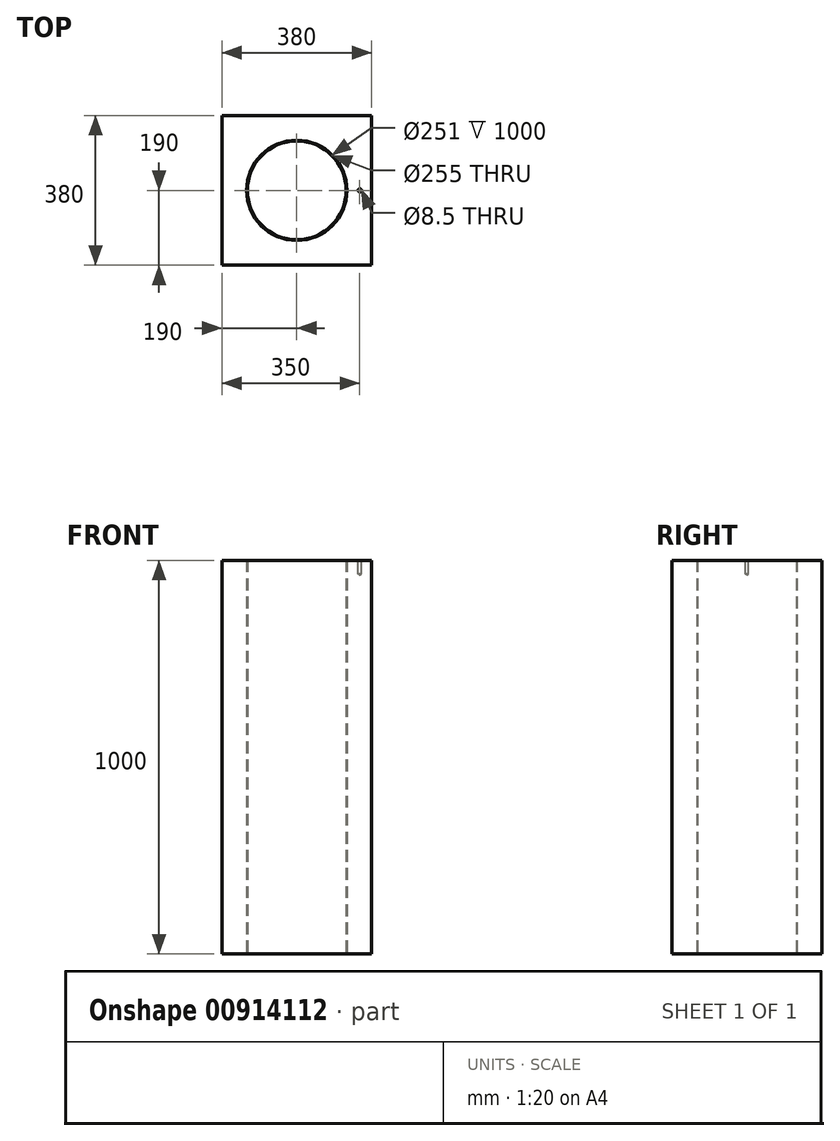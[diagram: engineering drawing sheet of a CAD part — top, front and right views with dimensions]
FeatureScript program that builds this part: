
annotation { "Feature Type Name" : "Feature", "Feature Type Description" : "" }
export const myFeature = defineFeature(function(context is Context, id is Id, definition is map)
    precondition{}
    {
        {
            var Q0;
            Q0=qCreatedBy(makeId("Top.planeOp"),FACE);
            var sketch = newSketch(context, id + "F0", { "sketchPlane" : qUnion([Q0])});
            skCircle(sketch, "E0", {"center": v(0, 0) * mm, "radius": 127.5 * mm});
            skLineSegment(sketch, "E1.bottom", {"start": v(190, -190) * mm, "end": v(-190, -190) * mm});
            skLineSegment(sketch, "E1.top", {"start": v(190, 190) * mm, "end": v(-190, 190) * mm});
            skLineSegment(sketch, "E1.left", {"start": v(190, -190) * mm, "end": v(190, 190) * mm});
            skLineSegment(sketch, "E1.right", {"start": v(-190, -190) * mm, "end": v(-190, 190) * mm});
            skSolve(sketch);
        }
        {
            var Q0;
            Q0=makeQuery(id+"F0.imprint","IMPRINT",FACE,{"disambiguationData":[TD([[makeQuery(id+"F0.imprint","IMPRINT",EDGE,{"derivedFrom":sQuery(id+"F0.wireOp",EDGE,"E0")}),-1.0]])]});
            extrude(context, id + "F1", {"entities" : qUnion([Q0]), "depth" : 1000 * mm, "offsetDistance" : 25 * mm});
        }
        {
            var Q0;
            Q0=makeQuery(id+"F1.opExtrude","CAP_FACE",FACE,{"disambiguationData":[OSD([sQuery(id+"F0.wireOp",EDGE,"E0"),sQuery(id+"F0.wireOp",EDGE,"11AzcM2P-MoAo-TPdU-SA0A-KGDendb4HZRf")])],"isStart":false});
            var sketch = newSketch(context, id + "F2", { "sketchPlane" : qUnion([Q0])});
            skPoint(sketch, "E2", {"position": v(160, 0) * mm});
            skLineSegment(sketch, "E3", {"start": v(127.5, 0) * mm, "end": v(190, 0) * mm, "construction": true});
            skSolve(sketch);
        }
        {
            var Q0;
            Q0=sQuery(id+"F2.wireOp",VERTEX,"E2");
            var Q1;
            Q1=makeQuery(id+"F1.opExtrude","SWEPT_BODY",BODY,{"disambiguationData":[OSD([sQuery(id+"F0.wireOp",EDGE,"E0"),sQuery(id+"F0.wireOp",EDGE,"11AzcM2P-MoAo-TPdU-SA0A-KGDendb4HZRf")])]});
            hole(context, id + "F3", {"style" : HoleStyle.SIMPLE, "endStyle" : HoleEndStyle.BLIND, "standardTappedOrClearance" : lookupTablePath({ "standard" : "ISO", "engagement" : "75%", "pitch" : "1.5 mm", "size" : "M10", "type" : "Tapped" }), "standardBlindInLast" : lookupTablePath({ "standard" : "ISO", "fit" : "Normal", "engagement" : "75%", "pitch" : "1.5 mm", "size" : "M10", "type" : "Clearance & tapped" }), "holeDiameter" : 8.5 * mm, "majorDiameter" : 10 * mm, "showTappedDepth" : true, "holeDepth" : 34.5 * mm, "isTappedThrough" : true, "tappedDepth" : 30 * mm, "tapClearance" : 3, "locations" : qUnion([Q0]), "scope" : qUnion([Q1])});
        }
        {
            var Q0;
            Q0=qCreatedBy(makeId("Top.planeOp"),FACE);
            var sketch = newSketch(context, id + "F4", { "sketchPlane" : qUnion([Q0])});
            skCircle(sketch, "E4.0", {"center": v(0, 0) * mm, "radius": 127.5 * mm});
            skCircle(sketch, "E5", {"center": v(0, 0) * mm, "radius": 125.5 * mm});
            skSolve(sketch);
        }
        {
            var Q0;
            Q0 = qSketchRegion(id + "F4", true);
            var Q1;
            Q1=makeQuery(id+"F1.opExtrude","CAP_FACE",FACE,{"disambiguationData":[OSD([sQuery(id+"F0.wireOp",EDGE,"E0"),sQuery(id+"F0.wireOp",EDGE,"E1.bottom"),sQuery(id+"F0.wireOp",EDGE,"E1.top"),sQuery(id+"F0.wireOp",EDGE,"E1.left"),sQuery(id+"F0.wireOp",EDGE,"E1.right")])],"isStart":false});
            extrude(context, id + "F5", {"entities" : qUnion([Q0]), "endBound" : BoundingType.UP_TO_SURFACE, "depth" : 25 * mm, "endBoundEntityFace" : qUnion([Q1]), "offsetDistance" : 25 * mm});
        }
    });
